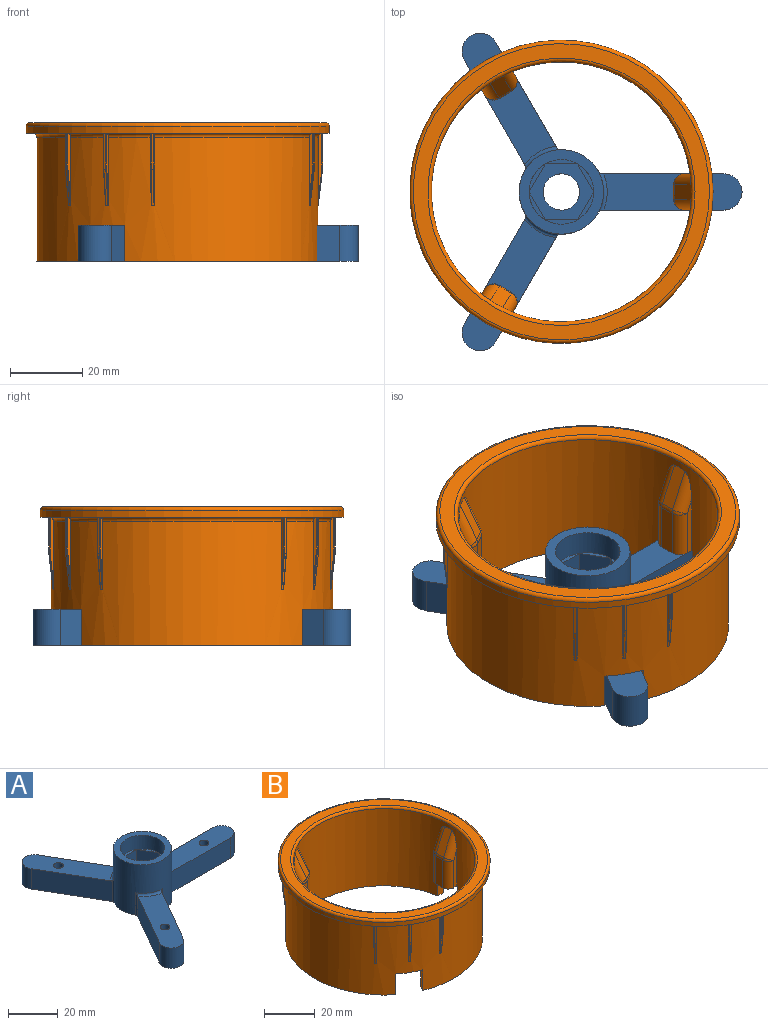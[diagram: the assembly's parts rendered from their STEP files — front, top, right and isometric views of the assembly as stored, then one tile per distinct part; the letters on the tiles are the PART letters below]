
ASSEMBLY  parts=2 mates=1
PART A: 42 faces, bbox 77.5x87.9x25 mm
  f0: plane 7.75x4.47mm, normal (0,0,1), area 7.3mm2, adj f16,f21
  f1: plane 8.95x1.2mm, normal (0,0,1), area 7.3mm2, adj f15,f21
  f2: plane 7.75x4.47mm, normal (0,0,1), area 7.3mm2, adj f14,f21
  f3: plane 7.75x4.47mm, normal (0,0,1), area 7.3mm2, adj f19,f21
  f4: plane 8.95x1.2mm, normal (0,0,1), area 7.3mm2, adj f18,f21
  f5: plane 7.75x4.47mm, normal (0,0,1), area 7.3mm2, adj f17,f21
  f6: plane 17.9x15.5mm, normal (0,0,1), area 128.9mm2, adj f9,f14,f15,f16,f17,f18,f19
  f7: plane 33.8x10.1mm, normal (0,1,0), area 338mm2, adj f11,f12,f13,f24,f25
  f8: plane 33.81x10.11mm, normal (0,-1,0), area 338mm2, adj f11,f12,f13,f23,f24
  f9: cylinder r=5.02mm len=10.04mm, axis (0,0,-1), area 315.4mm2, adj f6,f13
  f10: cylinder r=2mm len=10mm, axis (0,0,-1), area 125.7mm2, adj f12,f13
  f11: cylinder r=5mm len=10mm, axis (0,0,-1), area 157.1mm2, adj f7,f8,f12,f13
  f12: plane 38.32x10mm, normal (0,0,1), area 353mm2, adj f7,f8,f10,f11,f24
  f13: plane 87.94x77.5mm, normal (0,0,-1), area 1441.5mm2, adj f7,f8,f9,f10,f11,f20,f23,f25
  f14: plane 8.2x7.75mm, normal (0.87,-0.5,0), area 73.4mm2, adj f2,f6,f15,f19
  f15: plane 8.95x8.2mm, normal (0,-1,0), area 73.4mm2, adj f1,f6,f14,f16
  f16: plane 8.2x7.75mm, normal (-0.87,-0.5,0), area 73.4mm2, adj f0,f6,f15,f17
  f17: plane 8.2x7.75mm, normal (-0.87,0.5,0), area 73.4mm2, adj f5,f6,f16,f18
  f18: plane 8.95x8.2mm, normal (0,1,0), area 73.4mm2, adj f4,f6,f17,f19
  f19: plane 8.2x7.75mm, normal (0.87,0.5,0), area 73.4mm2, adj f3,f6,f14,f18
  f20: cylinder r=11.7mm len=25mm, axis (0,0,-1), area 1458.4mm2, adj f13,f22,f23,f24,f25,f31,f32,f33
  f21: cylinder r=8.95mm len=17.9mm, axis (0,0,-1), area 382.3mm2, adj f0,f1,f2,f3,f4,f5,f22
  f22: plane 23.41x23.41mm, normal (0,0,1), area 178.7mm2, adj f20,f21
  f23: cylinder r=1mm len=11mm, axis (0,0,-1), area 11.3mm2, adj f8,f13,f20,f24
  f24: torus R=12.7mm, axis (0,0,1), area 16.7mm2, adj f7,f8,f12,f20,f23,f25
  f25: cylinder r=1mm len=11mm, axis (0,0,-1), area 11.3mm2, adj f7,f13,f20,f24
  f26: cylinder r=2mm len=10mm, axis (0,0,-1), area 125.7mm2, adj f13,f29
  f27: cylinder r=5mm len=10mm, axis (0,0,-1), area 157.1mm2, adj f13,f28,f29,f30
  f28: plane 29.28x16.9mm, normal (-0.87,0.5,0), area 338mm2, adj f13,f27,f29,f32,f33
  f29: plane 36.36x25.99mm, normal (0,0,1), area 353mm2, adj f26,f27,f28,f30,f32
  f30: plane 29.28x16.9mm, normal (0.87,-0.5,0), area 338mm2, adj f13,f27,f29,f31,f32
  f31: cylinder r=1mm len=11mm, axis (0,0,-1), area 11.3mm2, adj f13,f20,f30,f32
  f32: torus R=12.7mm, axis (0,0,1), area 16.7mm2, adj f20,f28,f29,f30,f31,f33
  f33: cylinder r=1mm len=11mm, axis (0,0,-1), area 11.3mm2, adj f13,f20,f28,f32
  f34: plane 29.28x16.9mm, normal (-0.87,-0.5,0), area 338mm2, adj f13,f37,f38,f40,f41
  f35: plane 29.28x16.9mm, normal (0.87,0.5,0), area 338mm2, adj f13,f37,f38,f39,f40
  f36: cylinder r=2mm len=10mm, axis (0,0,-1), area 125.7mm2, adj f13,f38
  f37: cylinder r=5mm len=10mm, axis (0,0,-1), area 157.1mm2, adj f13,f34,f35,f38
  f38: plane 36.36x25.99mm, normal (0,0,1), area 353mm2, adj f34,f35,f36,f37,f40
  f39: cylinder r=1mm len=11mm, axis (0,0,-1), area 11.3mm2, adj f13,f20,f35,f40
  f40: torus R=12.7mm, axis (0,0,1), area 16.7mm2, adj f20,f34,f35,f38,f39,f41
  f41: cylinder r=1mm len=11mm, axis (0,0,-1), area 11.3mm2, adj f13,f20,f34,f40
PART B: 145 faces, bbox 91.2x91.2x38.7 mm
  f0: cylinder r=39mm len=78mm, axis (0,0,1), area 7926.9mm2, adj f2,f3,f4,f5,f6,f7,f8,f9
  f1: plane 84x84mm, normal (0,0,-1), area 513.5mm2, adj f2,f3,f4,f5,f6,f7,f8,f9
  f2: torus R=40mm, axis (0,0,-1), area 84.7mm2, adj f0,f1,f107,f114,f124,f127
  f3: torus R=40mm, axis (0,0,-1), area 20mm2, adj f0,f1,f116,f119,f123,f130
  f4: torus R=40mm, axis (0,0,-1), area 20mm2, adj f0,f1,f91,f98,f108,f111
  f5: torus R=40mm, axis (0,0,-1), area 84.7mm2, adj f0,f1,f83,f90,f100,f103
  f6: torus R=40mm, axis (0,0,-1), area 20mm2, adj f0,f1,f92,f95,f99,f106
  f7: torus R=40mm, axis (0,0,-1), area 20mm2, adj f0,f1,f67,f74,f84,f87
  f8: torus R=40mm, axis (0,0,-1), area 84.7mm2, adj f0,f1,f59,f66,f76,f79
  f9: torus R=40mm, axis (0,0,-1), area 20mm2, adj f0,f1,f68,f71,f75,f82
  f10: torus R=40mm, axis (0,0,-1), area 20mm2, adj f0,f1,f60,f63,f115,f122
  f11: plane 10.89x4.81mm, normal (-0.92,0,0.4), area 47.1mm2, adj f16,f19,f22,f51
  f12: plane 11x8mm, normal (0,0,-1), area 65.5mm2, adj f0,f13,f14,f15,f17,f18,f51,f57
  f13: plane 13.37x4mm, normal (-1,0,0), area 53.5mm2, adj f12,f17,f18,f22
  f14: plane 17.14x1.65mm, normal (0,-1,0), area 25.2mm2, adj f12,f16,f17,f51
  f15: plane 17.14x1.65mm, normal (0,1,0), area 25.2mm2, adj f12,f18,f19,f51
  f16: cylinder r=3mm len=11.9mm, axis (0.4,0,0.92), area 37.2mm2, adj f11,f14,f20,f51
  f17: cylinder r=3mm len=13.37mm, axis (0,0,1), area 63mm2, adj f12,f13,f14,f20
  f18: cylinder r=3mm len=13.37mm, axis (0,0,-1), area 63mm2, adj f12,f13,f15,f21
  f19: cylinder r=3mm len=11.9mm, axis (-0.4,0,-0.92), area 37.2mm2, adj f11,f15,f21,f51
  f20: sphere r=3mm, area 2.9mm2, adj f16,f17,f22
  f21: sphere r=3mm, area 2.9mm2, adj f18,f19,f22
  f22: cylinder r=3mm len=4mm, axis (0,1,0), area 5mm2, adj f11,f13,f20,f21
  f23: plane 11.08x6.32mm, normal (0.46,0.79,0.4), area 47.1mm2, adj f28,f31,f34,f51
  f24: plane 11.8x10.74mm, normal (0,0,-1), area 65.5mm2, adj f0,f25,f26,f27,f29,f30,f51,f55
  f25: plane 13.37x3.46mm, normal (0.5,0.87,0), area 53.5mm2, adj f24,f29,f30,f34
  f26: plane 17.14x1.43mm, normal (-0.87,0.5,0), area 25.2mm2, adj f24,f28,f29,f51
  f27: plane 17.14x1.43mm, normal (0.87,-0.5,0), area 25.2mm2, adj f24,f30,f31,f51
  f28: cylinder r=3mm len=11.9mm, axis (-0.2,-0.35,0.92), area 37.2mm2, adj f23,f26,f32,f51
  f29: cylinder r=3mm len=13.37mm, axis (0,0,1), area 63mm2, adj f24,f25,f26,f32
  f30: cylinder r=3mm len=13.37mm, axis (0,0,-1), area 63mm2, adj f24,f25,f27,f33
  f31: cylinder r=3mm len=11.9mm, axis (0.2,0.35,-0.92), area 37.2mm2, adj f23,f27,f33,f51
  f32: sphere r=3mm, area 2.9mm2, adj f28,f29,f34
  f33: sphere r=3mm, area 2.9mm2, adj f30,f31,f34
  f34: cylinder r=3mm len=3.59mm, axis (0.87,-0.5,0), area 5mm2, adj f23,f25,f32,f33
  f35: plane 11.08x6.32mm, normal (0.46,-0.79,0.4), area 47.1mm2, adj f40,f43,f46,f51
  f36: plane 11.8x10.74mm, normal (0,0,-1), area 65.5mm2, adj f0,f37,f38,f39,f41,f42,f51,f53
  f37: plane 13.37x3.46mm, normal (0.5,-0.87,0), area 53.5mm2, adj f36,f41,f42,f46
  f38: plane 17.14x1.43mm, normal (0.87,0.5,0), area 25.2mm2, adj f36,f40,f41,f51
  f39: plane 17.14x1.43mm, normal (-0.87,-0.5,0), area 25.2mm2, adj f36,f42,f43,f51
  f40: cylinder r=3mm len=11.9mm, axis (-0.2,0.35,0.92), area 37.2mm2, adj f35,f38,f44,f51
  f41: cylinder r=3mm len=13.37mm, axis (0,0,1), area 63mm2, adj f36,f37,f38,f44
  f42: cylinder r=3mm len=13.37mm, axis (0,0,-1), area 63mm2, adj f36,f37,f39,f45
  f43: cylinder r=3mm len=11.9mm, axis (0.2,-0.35,-0.92), area 37.2mm2, adj f35,f39,f45,f51
  f44: sphere r=3mm, area 2.9mm2, adj f40,f41,f46
  f45: sphere r=3mm, area 2.9mm2, adj f42,f43,f46
  f46: cylinder r=3mm len=3.59mm, axis (-0.87,-0.5,0), area 5mm2, adj f35,f37,f44,f45
  f47: plane 53.15x33.5mm, normal (0,0,-1), area 202.5mm2, adj f0,f51,f54,f57
  f48: plane 53.15x33.5mm, normal (0,0,-1), area 202.5mm2, adj f0,f51,f55,f58
  f49: plane 61.38x16.45mm, normal (0,0,-1), area 202.5mm2, adj f0,f51,f53,f56
  f50: plane 82x82mm, normal (0,0,1), area 980.2mm2, adj f131,f132
  f51: cylinder r=36mm len=72mm, axis (0,0,1), area 7401.7mm2, adj f11,f12,f14,f15,f16,f19,f23,f24
  f52: cylinder r=42mm len=84mm, axis (0,0,1), area 527.8mm2, adj f1,f132
  f53: plane 10x2.63mm, normal (0.87,0.5,0), area 30.3mm2, adj f0,f36,f49,f51
  f54: plane 10x2.63mm, normal (-0.87,-0.5,0), area 30.3mm2, adj f0,f36,f47,f51
  f55: plane 10x2.63mm, normal (-0.87,0.5,0), area 30.3mm2, adj f0,f24,f48,f51
  f56: plane 10x2.63mm, normal (0.87,-0.5,0), area 30.3mm2, adj f0,f24,f49,f51
  f57: plane 10x3.03mm, normal (0,-1,0), area 30.3mm2, adj f0,f12,f47,f51
  f58: plane 10x3.03mm, normal (0,1,0), area 30.3mm2, adj f0,f12,f48,f51
  f59: plane 18.29x0.99mm, normal (0.99,0.16,0), area 13.9mm2, adj f0,f8,f65,f66
  f60: plane 18.29x0.98mm, normal (-0.98,-0.19,0), area 13.9mm2, adj f0,f10,f63,f64
  f61: cone r=39mm half-angle=6.8deg, axis (0,0,1), area 6.5mm2, adj f0,f62,f64,f65
  f62: cylinder r=40.2mm len=9.86mm, axis (0,0,1), area 6.4mm2, adj f1,f61,f63,f66
  f63: cylinder r=0.2mm len=9.86mm, axis (0,0,1), area 3.1mm2, adj f1,f10,f60,f62,f64
  f64: bspline ~27.8x3.46mm, area 2.9mm2, adj f0,f60,f61,f63
  f65: bspline ~27.8x3.44mm, area 2.9mm2, adj f0,f59,f61,f66
  f66: cylinder r=0.2mm len=9.86mm, axis (0,0,1), area 3.1mm2, adj f1,f8,f59,f62,f65
  f67: plane 18.29x1mm, normal (-0.01,-1,0), area 13.9mm2, adj f0,f7,f73,f74
  f68: plane 18.29x1mm, normal (-0.01,1,0), area 13.9mm2, adj f0,f9,f71,f72
  f69: cone r=39mm half-angle=6.8deg, axis (0,0,1), area 6.5mm2, adj f0,f70,f72,f73
  f70: cylinder r=40.2mm len=9.86mm, axis (0,0,1), area 6.4mm2, adj f1,f69,f71,f74
  f71: cylinder r=0.2mm len=9.86mm, axis (0,0,1), area 3.1mm2, adj f1,f9,f68,f70,f72
  f72: bspline ~27.8x3.49mm, area 2.9mm2, adj f0,f68,f69,f71
  f73: bspline ~27.8x3.49mm, area 2.9mm2, adj f0,f67,f69,f74
  f74: cylinder r=0.2mm len=9.86mm, axis (0,0,1), area 3.1mm2, adj f1,f7,f67,f70,f73
  f75: plane 18.29x0.94mm, normal (0.33,-0.94,0), area 13.9mm2, adj f0,f9,f81,f82
  f76: plane 18.29x0.93mm, normal (-0.35,0.94,0), area 13.9mm2, adj f0,f8,f79,f80
  f77: cone r=39mm half-angle=6.8deg, axis (0,0,1), area 6.5mm2, adj f0,f78,f80,f81
  f78: cylinder r=40.2mm len=9.86mm, axis (0,0,1), area 6.4mm2, adj f1,f77,f79,f82
  f79: cylinder r=0.2mm len=9.86mm, axis (0,0,1), area 3.1mm2, adj f1,f8,f76,f78,f80
  f80: bspline ~27.8x3.33mm, area 2.9mm2, adj f0,f76,f77,f79
  f81: bspline ~27.8x3.29mm, area 2.9mm2, adj f0,f75,f77,f82
  f82: cylinder r=0.2mm len=9.86mm, axis (0,0,1), area 3.1mm2, adj f1,f9,f75,f78,f81
  f83: plane 18.29x0.93mm, normal (-0.35,-0.94,0), area 13.9mm2, adj f0,f5,f89,f90
  f84: plane 18.29x0.94mm, normal (0.33,0.94,0), area 13.9mm2, adj f0,f7,f87,f88
  f85: cone r=39mm half-angle=6.8deg, axis (0,0,1), area 6.5mm2, adj f0,f86,f88,f89
  f86: cylinder r=40.2mm len=9.86mm, axis (0,0,1), area 6.4mm2, adj f1,f85,f87,f90
  f87: cylinder r=0.2mm len=9.86mm, axis (0,0,1), area 3.1mm2, adj f1,f7,f84,f86,f88
  f88: bspline ~27.8x3.29mm, area 2.9mm2, adj f0,f84,f85,f87
  f89: bspline ~27.8x3.33mm, area 2.9mm2, adj f0,f83,f85,f90
  f90: cylinder r=0.2mm len=9.86mm, axis (0,0,1), area 3.1mm2, adj f1,f5,f83,f86,f89
  f91: plane 18.29x0.86mm, normal (-0.86,0.51,0), area 13.9mm2, adj f0,f4,f97,f98
  f92: plane 18.29x0.87mm, normal (0.87,-0.49,0), area 13.9mm2, adj f0,f6,f95,f96
  f93: cone r=39mm half-angle=6.8deg, axis (0,0,1), area 6.5mm2, adj f0,f94,f96,f97
  f94: cylinder r=40.2mm len=9.86mm, axis (0,0,1), area 6.4mm2, adj f1,f93,f95,f98
  f95: cylinder r=0.2mm len=9.86mm, axis (0,0,1), area 3.1mm2, adj f1,f6,f92,f94,f96
  f96: bspline ~27.8x3.04mm, area 2.9mm2, adj f0,f92,f93,f95
  f97: bspline ~27.8x3.1mm, area 2.9mm2, adj f0,f91,f93,f98
  f98: cylinder r=0.2mm len=9.86mm, axis (0,0,1), area 3.1mm2, adj f1,f4,f91,f94,f97
  f99: plane 18.29x0.98mm, normal (-0.98,0.19,0), area 13.9mm2, adj f0,f6,f105,f106
  f100: plane 18.29x0.99mm, normal (0.99,-0.16,0), area 13.9mm2, adj f0,f5,f103,f104
  f101: cone r=39mm half-angle=6.8deg, axis (0,0,1), area 6.5mm2, adj f0,f102,f104,f105
  f102: cylinder r=40.2mm len=9.86mm, axis (0,0,1), area 6.4mm2, adj f1,f101,f103,f106
  f103: cylinder r=0.2mm len=9.86mm, axis (0,0,1), area 3.1mm2, adj f1,f5,f100,f102,f104
  f104: bspline ~27.8x3.44mm, area 2.9mm2, adj f0,f100,f101,f103
  f105: bspline ~27.8x3.46mm, area 2.9mm2, adj f0,f99,f101,f106
  f106: cylinder r=0.2mm len=9.86mm, axis (0,0,1), area 3.1mm2, adj f1,f6,f99,f102,f105
  f107: plane 18.29x0.77mm, normal (-0.63,0.77,0), area 13.9mm2, adj f0,f2,f113,f114
  f108: plane 18.29x0.76mm, normal (0.65,-0.76,0), area 13.9mm2, adj f0,f4,f111,f112
  f109: cone r=39mm half-angle=6.8deg, axis (0,0,1), area 6.5mm2, adj f0,f110,f112,f113
  f110: cylinder r=40.2mm len=9.86mm, axis (0,0,1), area 6.4mm2, adj f1,f109,f111,f114
  f111: cylinder r=0.2mm len=9.86mm, axis (0,0,1), area 3.1mm2, adj f1,f4,f108,f110,f112
  f112: bspline ~27.8x2.77mm, area 2.9mm2, adj f0,f108,f109,f111
  f113: bspline ~27.8x2.7mm, area 2.9mm2, adj f0,f107,f109,f114
  f114: cylinder r=0.2mm len=9.86mm, axis (0,0,1), area 3.1mm2, adj f1,f2,f107,f110,f113
  f115: plane 18.29x0.87mm, normal (0.87,0.49,0), area 13.9mm2, adj f0,f10,f121,f122
  f116: plane 18.29x0.86mm, normal (-0.86,-0.51,0), area 13.9mm2, adj f0,f3,f119,f120
  f117: cone r=39mm half-angle=6.8deg, axis (0,0,1), area 6.5mm2, adj f0,f118,f120,f121
  f118: cylinder r=40.2mm len=9.86mm, axis (0,0,1), area 6.4mm2, adj f1,f117,f119,f122
  f119: cylinder r=0.2mm len=9.86mm, axis (0,0,1), area 3.1mm2, adj f1,f3,f116,f118,f120
  f120: bspline ~27.8x3.1mm, area 2.9mm2, adj f0,f116,f117,f119
  f121: bspline ~27.8x3.04mm, area 2.9mm2, adj f0,f115,f117,f122
  f122: cylinder r=0.2mm len=9.86mm, axis (0,0,1), area 3.1mm2, adj f1,f10,f115,f118,f121
  f123: plane 18.29x0.76mm, normal (0.65,0.76,0), area 13.9mm2, adj f0,f3,f129,f130
  f124: plane 18.29x0.77mm, normal (-0.63,-0.77,0), area 13.9mm2, adj f0,f2,f127,f128
  f125: cone r=39mm half-angle=6.8deg, axis (0,0,1), area 6.5mm2, adj f0,f126,f128,f129
  f126: cylinder r=40.2mm len=9.86mm, axis (0,0,1), area 6.4mm2, adj f1,f125,f127,f130
  f127: cylinder r=0.2mm len=9.86mm, axis (0,0,1), area 3.1mm2, adj f1,f2,f124,f126,f128
  f128: bspline ~27.8x2.7mm, area 2.9mm2, adj f0,f124,f125,f127
  f129: bspline ~27.8x2.77mm, area 2.9mm2, adj f0,f123,f125,f130
  f130: cylinder r=0.2mm len=9.86mm, axis (0,0,1), area 3.1mm2, adj f1,f3,f123,f126,f129
  f131: torus R=37mm, axis (0,0,1), area 358.9mm2, adj f50,f51
  f132: torus R=41mm, axis (0,0,1), area 410.9mm2, adj f50,f52
  f133: plane 7.04x4.19mm, normal (-0.46,0.79,-0.4), area 25mm2, adj f134,f136
  f134: cylinder r=36mm len=3.04mm, axis (0,0,1), area 7.4mm2, adj f133,f135,f136
  f135: torus R=37mm, axis (0,0,1), area 1460.7mm2, adj f134,f136
  f136: cylinder r=2mm len=24.4mm, axis (0,0,-1), area 255.2mm2, adj f36,f133,f134,f135
  f137: plane 7.04x4.19mm, normal (-0.46,-0.79,-0.4), area 25mm2, adj f138,f140
  f138: cylinder r=36mm len=3.04mm, axis (0,0,1), area 7.4mm2, adj f137,f139,f140
  f139: torus R=37mm, axis (0,0,1), area 1460.7mm2, adj f138,f140
  f140: cylinder r=2mm len=24.4mm, axis (0,0,-1), area 255.2mm2, adj f24,f137,f138,f139
  f141: plane 7.04x4.2mm, normal (0.92,0,-0.4), area 25mm2, adj f142,f144
  f142: cylinder r=36mm len=3.51mm, axis (0,0,1), area 7.4mm2, adj f141,f143,f144
  f143: torus R=37mm, axis (0,0,1), area 1460.7mm2, adj f142,f144
  f144: cylinder r=2mm len=24.4mm, axis (0,0,-1), area 255.2mm2, adj f12,f141,f142,f143
PLACE A t=(15.17,17.31,14.19)mm
PLACE B t=(15.17,17.31,52.59)mm
MATE fastened B.f136 <-> A.f36  axis (0,0,-1) through (-2.33,47.62,24.19)mm
